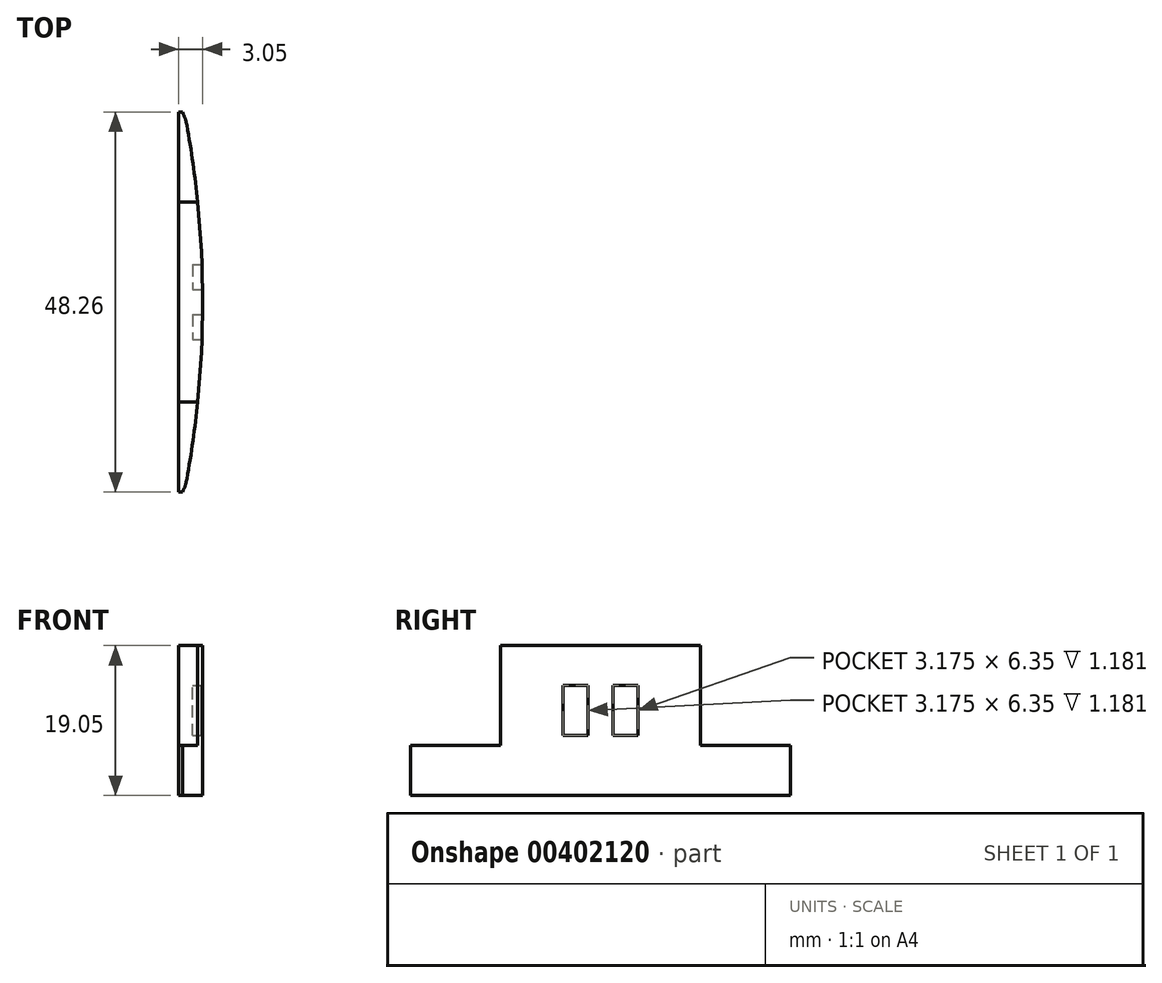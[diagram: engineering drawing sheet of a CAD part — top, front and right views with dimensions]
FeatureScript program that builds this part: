
annotation { "Feature Type Name" : "Feature", "Feature Type Description" : "" }
export const myFeature = defineFeature(function(context is Context, id is Id, definition is map)
    precondition{}
    {
        {
            var Q0;
            Q0=qCreatedBy(makeId("Top.planeOp"),FACE);
            var sketch = newSketch(context, id + "F0", { "sketchPlane" : qUnion([Q0])});
            skArc(sketch, "E0", {"start": v(-3.07, -27.77) * mm, "mid": v(0, 0) * mm, "end": v(-3.07, 27.77) * mm});
            skLineSegment(sketch, "E1", {"start": v(-3.07, 27.77) * mm, "end": v(-3.07, -27.77) * mm});
            skLineSegment(sketch, "E2", {"start": v(0, 0) * mm, "end": v(14.93, 0) * mm, "construction": true});
            skLineSegment(sketch, "E3", {"start": v(0, 27.81) * mm, "end": v(0, -27.81) * mm});
            skLineSegment(sketch, "E4", {"start": v(0, 27.81) * mm, "end": v(-15.77, 27.6) * mm});
            skLineSegment(sketch, "E5", {"start": v(0, -27.81) * mm, "end": v(-15.77, -27.6) * mm});
            skLineSegment(sketch, "E6", {"start": v(-15.77, 27.6) * mm, "end": v(-15.77, -27.6) * mm});
            skSolve(sketch);
        }
        {
            var Q0;
            Q0=makeQuery(id+"F0.imprint","IMPRINT",FACE,{"disambiguationData":[TD([[makeQuery(id+"F0.imprint","IMPRINT",EDGE,{"derivedFrom":sQuery(id+"F0.wireOp",EDGE,"E0")}),1.0]])]});
            var Q1;
            {var subQ0=sQuery(id+"F0.wireOp",EDGE,"E1");Q1=makeQuery(id+"F0.imprint","IMPRINT",FACE,{"disambiguationData":[TD([[makeQuery(id+"F0.imprint","IMPRINT",EDGE,{"derivedFrom":subQ0}),-1.0]])]});}
            extrude(context, id + "F1", {"entities" : qUnion([Q0, Q1]), "depth" : 25.4 * mm});
        }
        {
            var Q0;
            Q0=makeQuery(id+"F1.opExtrude","SWEPT_EDGE",EDGE,{"disambiguationData":[OSD([sQuery(id+"F0.wireOp",EDGE,"E0"),sQuery(id+"F0.wireOp",EDGE,"E1"),sQuery(id+"F0.wireOp",EDGE,"E4")])]});
            var Q1;
            Q1=makeQuery(id+"F1.opExtrude","SWEPT_EDGE",EDGE,{"disambiguationData":[OSD([sQuery(id+"F0.wireOp",EDGE,"E0"),sQuery(id+"F0.wireOp",EDGE,"E1"),sQuery(id+"F0.wireOp",EDGE,"E5")])]});
            fillet(context, id + "F2", {"entities" : qUnion([Q0, Q1]), "radius" : 6.35 * mm, "tangentPropagation" : true, "allowEdgeOverflow" : false});
        }
        {
            var Q0;
            Q0=qCreatedBy(makeId("Right.planeOp"),FACE);
            var sketch = newSketch(context, id + "F3", { "sketchPlane" : qUnion([Q0])});
            skLineSegment(sketch, "E7.bottom", {"start": v(-12.7, 22.86) * mm, "end": v(12.7, 22.86) * mm});
            skLineSegment(sketch, "E7.top", {"start": v(-12.7, 10.16) * mm, "end": v(12.7, 10.16) * mm});
            skLineSegment(sketch, "E7.left", {"start": v(-12.7, 22.86) * mm, "end": v(-12.7, 10.16) * mm});
            skLineSegment(sketch, "E7.right", {"start": v(12.7, 22.86) * mm, "end": v(12.7, 10.16) * mm});
            skPoint(sketch, "E7.middle", {"position": v(0, 16.51) * mm});
            skLineSegment(sketch, "E8.bottom", {"start": v(-24.13, 10.16) * mm, "end": v(24.13, 10.16) * mm});
            skLineSegment(sketch, "E8.top", {"start": v(-24.13, 3.81) * mm, "end": v(24.13, 3.81) * mm});
            skLineSegment(sketch, "E8.left", {"start": v(-24.13, 10.16) * mm, "end": v(-24.13, 3.81) * mm});
            skLineSegment(sketch, "E8.right", {"start": v(24.13, 10.16) * mm, "end": v(24.13, 3.81) * mm});
            skPoint(sketch, "E8.middle", {"position": v(0, 6.99) * mm});
            skLineSegment(sketch, "E9.bottom", {"start": v(-30.13, 27.75) * mm, "end": v(35.68, 27.75) * mm});
            skLineSegment(sketch, "E9.top", {"start": v(-30.13, -6.99) * mm, "end": v(35.68, -6.99) * mm});
            skLineSegment(sketch, "E9.left", {"start": v(-30.13, 27.75) * mm, "end": v(-30.13, -6.99) * mm});
            skLineSegment(sketch, "E9.right", {"start": v(35.68, 27.75) * mm, "end": v(35.68, -6.99) * mm});
            skSolve(sketch);
        }
        {
            var Q0;
            Q0=qSketchRegion(id+"F3",true);
            extrude(context, id + "F4", {"entities" : qUnion([Q0]), "operationType" : NewBodyOperationType.REMOVE, "endBound" : BoundingType.THROUGH_ALL, "oppositeDirection" : true, "depth" : 25.4 * mm});
        }
        {
            var Q0;
            Q0=qCreatedBy(makeId("Top.planeOp"),FACE);
            var sketch = newSketch(context, id + "F5", { "sketchPlane" : qUnion([Q0])});
            skLineSegment(sketch, "E10.bottom", {"start": v(0, -27.1) * mm, "end": v(-3.05, -27.1) * mm});
            skLineSegment(sketch, "E10.top", {"start": v(0, 25.43) * mm, "end": v(-3.05, 25.43) * mm});
            skLineSegment(sketch, "E10.left", {"start": v(0, -27.1) * mm, "end": v(0, 25.43) * mm});
            skLineSegment(sketch, "E10.right", {"start": v(-3.05, -27.1) * mm, "end": v(-3.05, 25.43) * mm});
            skLineSegment(sketch, "E11.bottom", {"start": v(-3.05, -27.1) * mm, "end": v(-16.7, -27.1) * mm});
            skLineSegment(sketch, "E11.top", {"start": v(-3.05, 25.43) * mm, "end": v(-16.7, 25.43) * mm});
            skLineSegment(sketch, "E11.right", {"start": v(-16.7, -27.1) * mm, "end": v(-16.7, 25.43) * mm});
            skSolve(sketch);
        }
        {
            var Q0;
            Q0=makeQuery(id+"F5.imprint","IMPRINT",FACE,{"disambiguationData":[TD([[makeQuery(id+"F5.imprint","IMPRINT",EDGE,{"derivedFrom":sQuery(id+"F5.wireOp",EDGE,"E11.bottom")}),-1.0]])]});
            extrude(context, id + "F6", {"entities" : qUnion([Q0]), "operationType" : NewBodyOperationType.REMOVE, "endBound" : BoundingType.THROUGH_ALL, "depth" : 25.4 * mm});
        }
        {
            var Q0;
            Q0=qCreatedBy(makeId("Right.planeOp"),FACE);
            var sketch = newSketch(context, id + "F7", { "sketchPlane" : qUnion([Q0])});
            skLineSegment(sketch, "E12", {"start": v(0, 0) * mm, "end": v(0, 8) * mm, "construction": true});
            skLineSegment(sketch, "E13.bottom", {"start": v(-1.59, 11.43) * mm, "end": v(-4.76, 11.43) * mm});
            skLineSegment(sketch, "E13.top", {"start": v(-1.59, 17.78) * mm, "end": v(-4.76, 17.78) * mm});
            skLineSegment(sketch, "E13.left", {"start": v(-1.59, 11.43) * mm, "end": v(-1.59, 17.78) * mm});
            skLineSegment(sketch, "E13.right", {"start": v(-4.76, 11.43) * mm, "end": v(-4.76, 17.78) * mm});
            skPoint(sketch, "E13.middle", {"position": v(-3.18, 14.6) * mm});
            skLineSegment(sketch, "E14.bottom", {"start": v(4.76, 11.43) * mm, "end": v(1.59, 11.43) * mm});
            skLineSegment(sketch, "E14.top", {"start": v(4.76, 17.78) * mm, "end": v(1.59, 17.78) * mm});
            skLineSegment(sketch, "E14.left", {"start": v(4.76, 11.43) * mm, "end": v(4.76, 17.78) * mm});
            skLineSegment(sketch, "E14.right", {"start": v(1.59, 11.43) * mm, "end": v(1.59, 17.78) * mm});
            skPoint(sketch, "E14.middle", {"position": v(3.18, 14.6) * mm});
            skSolve(sketch);
        }
        {
            var Q0;
            Q0=qSketchRegion(id+"F7",true);
            extrude(context, id + "F8", {"entities" : qUnion([Q0]), "operationType" : NewBodyOperationType.REMOVE, "oppositeDirection" : true, "depth" : 1.27 * mm});
        }
    });
